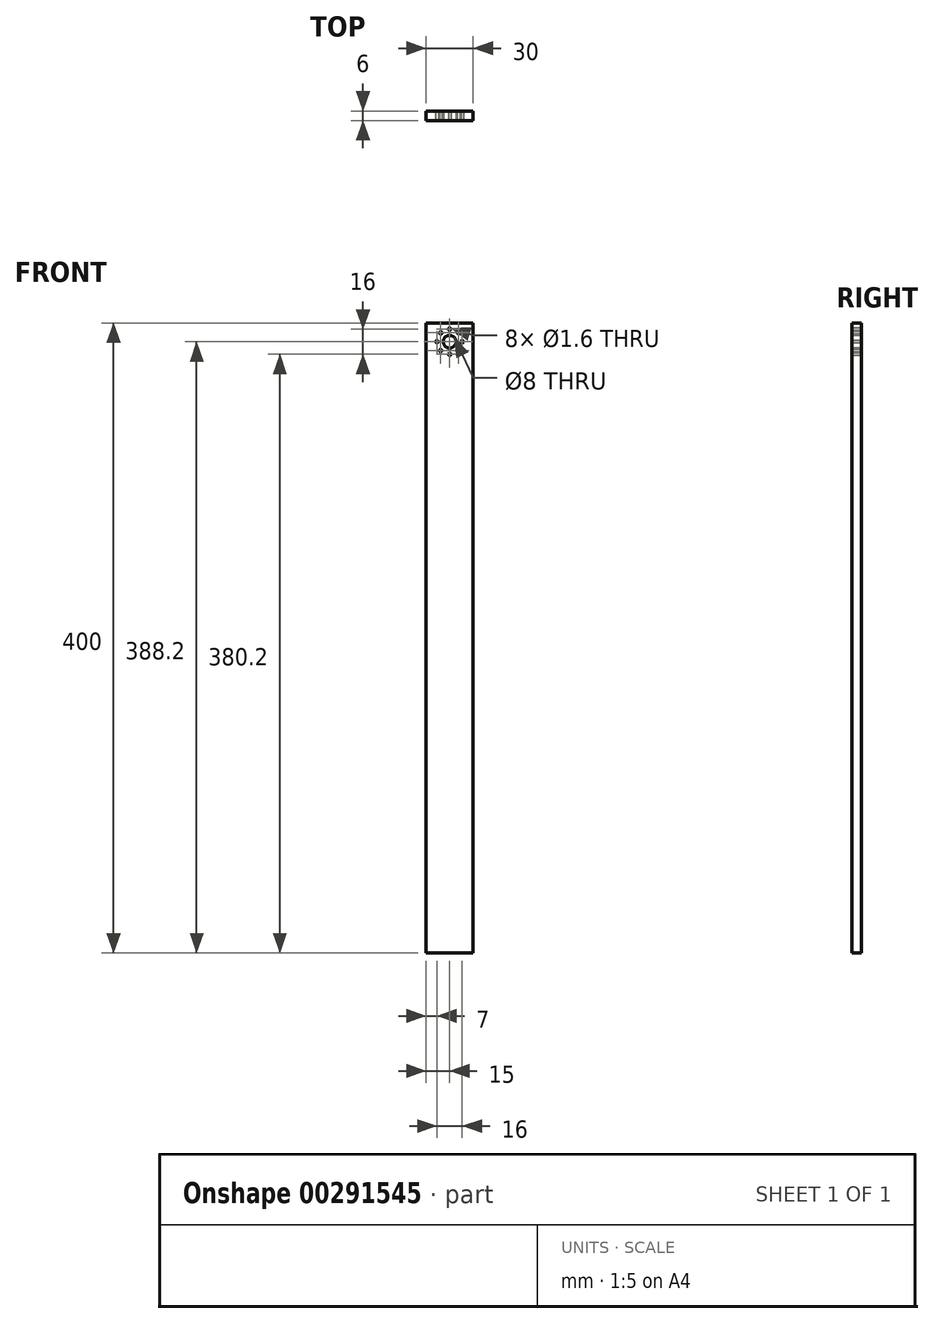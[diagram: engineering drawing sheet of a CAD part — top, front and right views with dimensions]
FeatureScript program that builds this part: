
annotation { "Feature Type Name" : "Feature", "Feature Type Description" : "" }
export const myFeature = defineFeature(function(context is Context, id is Id, definition is map)
    precondition{}
    {
        {
            var Q0;
            Q0=qCreatedBy(makeId("Top.planeOp"),FACE);
            var sketch = newSketch(context, id + "F0", { "sketchPlane" : qUnion([Q0])});
            skLineSegment(sketch, "E0.bottom", {"start": v(-15, 3) * mm, "end": v(15, 3) * mm});
            skLineSegment(sketch, "E0.top", {"start": v(-15, -3) * mm, "end": v(15, -3) * mm});
            skLineSegment(sketch, "E0.left", {"start": v(-15, 3) * mm, "end": v(-15, -3) * mm});
            skLineSegment(sketch, "E0.right", {"start": v(15, 3) * mm, "end": v(15, -3) * mm});
            skSolve(sketch);
        }
        {
            var Q0;
            Q0 = qSketchRegion(id + "F0", true);
            extrude(context, id + "F1", {"entities" : qUnion([Q0]), "endBound" : BoundingType.SYMMETRIC, "depth" : 400 * mm, "offsetDistance" : 25 * mm});
        }
        {
            var Q0;
            Q0=makeQuery(id+"F1.opExtrude","SWEPT_FACE",FACE,{"disambiguationData":[OSD([sQuery(id+"F0.wireOp",EDGE,"E0.top")])]});
            var sketch = newSketch(context, id + "F2", { "sketchPlane" : qUnion([Q0])});
            skCircle(sketch, "E1", {"center": v(0, 196.2) * mm, "radius": 0.8 * mm});
            skCircle(sketch, "E2", {"center": v(0, 188.2) * mm, "radius": 4 * mm});
            skCircle(sketch, "E3.1.0", {"center": v(-5.66, 193.86) * mm, "radius": 0.8 * mm});
            skCircle(sketch, "E3.2.0", {"center": v(-8, 188.2) * mm, "radius": 0.8 * mm});
            skCircle(sketch, "E3.3.0", {"center": v(-5.66, 182.54) * mm, "radius": 0.8 * mm});
            skCircle(sketch, "E3.4.0", {"center": v(0, 180.2) * mm, "radius": 0.8 * mm});
            skCircle(sketch, "E3.5.0", {"center": v(5.66, 182.54) * mm, "radius": 0.8 * mm});
            skCircle(sketch, "E3.6.0", {"center": v(8, 188.2) * mm, "radius": 0.8 * mm});
            skCircle(sketch, "E3.7.0", {"center": v(5.66, 193.86) * mm, "radius": 0.8 * mm});
            skSolve(sketch);
        }
        {
            var Q0;
            Q0 = qSketchRegion(id + "F2", true);
            extrude(context, id + "F3", {"entities" : qUnion([Q0]), "operationType" : NewBodyOperationType.REMOVE, "endBound" : BoundingType.UP_TO_NEXT, "oppositeDirection" : true, "depth" : 25 * mm});
        }
    });
